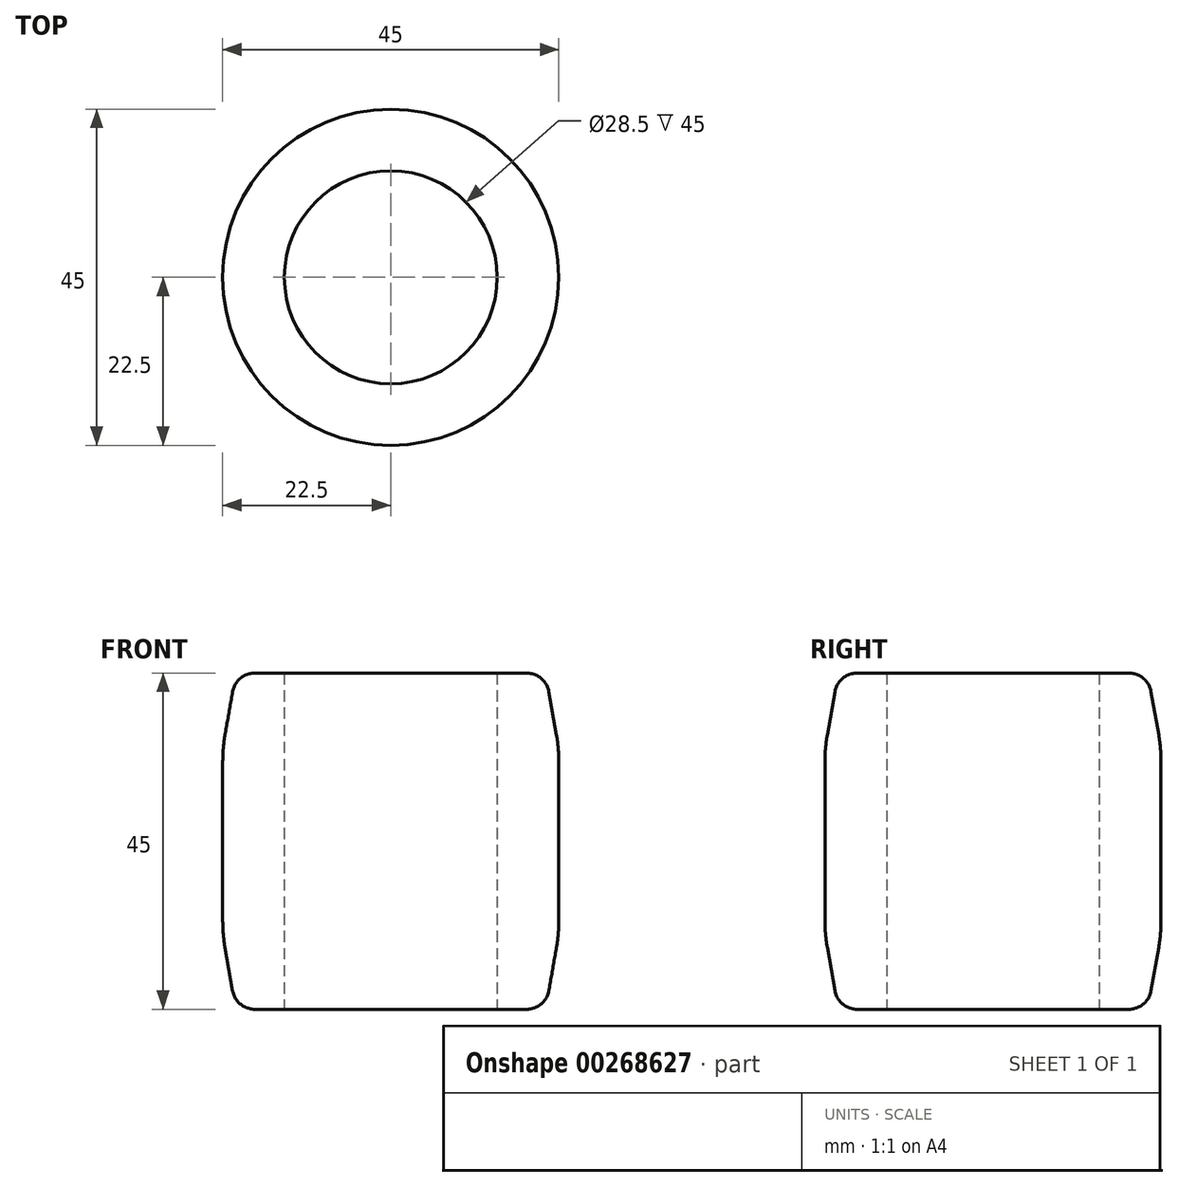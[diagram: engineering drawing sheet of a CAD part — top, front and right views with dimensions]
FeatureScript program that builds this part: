
annotation { "Feature Type Name" : "Feature", "Feature Type Description" : "" }
export const myFeature = defineFeature(function(context is Context, id is Id, definition is map)
    precondition{}
    {
        {
            var Q0;
            Q0=qCreatedBy(makeId("Top.planeOp"),FACE);
            var sketch = newSketch(context, id + "F0", { "sketchPlane" : qUnion([Q0])});
            skCircle(sketch, "E0", {"center": v(0, 0) * mm, "radius": 22.5 * mm});
            skCircle(sketch, "E1", {"center": v(0, 0) * mm, "radius": 14.25 * mm});
            skSolve(sketch);
        }
        {
            var Q0;
            Q0=makeQuery(id+"F0.imprint","IMPRINT",FACE,{"disambiguationData":[TD([[makeQuery(id+"F0.imprint","IMPRINT",EDGE,{"derivedFrom":sQuery(id+"F0.wireOp",EDGE,"E0")}),1.0]])]});
            extrude(context, id + "F1", {"entities" : qUnion([Q0]), "depth" : 45 * mm, "offsetDistance" : 25 * mm});
        }
        {
            var Q0;
            Q0=makeQuery(id+"F1.opExtrude","CAP_EDGE",EDGE,{"disambiguationData":[OSD([sQuery(id+"F0.wireOp",EDGE,"E0")])],"isStart":true});
            var Q1;
            Q1=makeQuery(id+"F1.opExtrude","CAP_EDGE",EDGE,{"disambiguationData":[OSD([sQuery(id+"F0.wireOp",EDGE,"E0")])],"isStart":false});
            chamfer(context, id + "F2", {"entities" : qUnion([Q0, Q1]), "chamferType" : ChamferType.OFFSET_ANGLE, "width" : 10 * mm, "oppositeDirection" : false, "angle" : 10 * degree, "tangentPropagation" : true});
        }
        {
            var Q0;
            Q0=makeQuery(id+"F1.opExtrude","SWEPT_FACE",FACE,{"disambiguationData":[OSD([sQuery(id+"F0.wireOp",EDGE,"E0")])]});
            var Q1;
            {var subQ0=sQuery(id+"F0.wireOp",EDGE,"E0");Q1=makeQuery(id+"F2.opChamfer","BLEND_EDGE",EDGE,{"blendedFrom":[makeQuery(id+"F1.opExtrude","CAP_EDGE",EDGE,{"disambiguationData":[OSD([subQ0])],"isStart":true}),makeQuery(id+"F1.opExtrude","SWEPT_FACE",FACE,{"disambiguationData":[OSD([subQ0])]})],"blendedInto":[makeQuery(id+"F1.opExtrude","SWEPT_FACE",FACE,{"disambiguationData":[OSD([subQ0])]})]});}
            fillet(context, id + "F3", {"entities" : qUnion([Q0, Q1]), "radius" : 20 * mm, "tangentPropagation" : true, "allowEdgeOverflow" : false});
        }
        {
            var Q0;
            {var subQ0=sQuery(id+"F0.wireOp",EDGE,"E0");Q0=makeQuery(id+"F2.opChamfer","BLEND_EDGE",EDGE,{"blendedFrom":[makeQuery(id+"F1.opExtrude","CAP_EDGE",EDGE,{"disambiguationData":[OSD([subQ0])],"isStart":false}),makeQuery(id+"F1.opExtrude","CAP_FACE",FACE,{"disambiguationData":[OSD([subQ0,sQuery(id+"F0.wireOp",EDGE,"E1")])],"isStart":false})],"blendedInto":[makeQuery(id+"F1.opExtrude","CAP_FACE",FACE,{"disambiguationData":[OSD([subQ0,sQuery(id+"F0.wireOp",EDGE,"E1")])],"isStart":false})]});}
            var Q1;
            {var subQ0=sQuery(id+"F0.wireOp",EDGE,"E0");Q1=makeQuery(id+"F2.opChamfer","BLEND_EDGE",EDGE,{"blendedFrom":[makeQuery(id+"F1.opExtrude","CAP_EDGE",EDGE,{"disambiguationData":[OSD([subQ0])],"isStart":true}),makeQuery(id+"F1.opExtrude","CAP_FACE",FACE,{"disambiguationData":[OSD([subQ0,sQuery(id+"F0.wireOp",EDGE,"E1")])],"isStart":true})],"blendedInto":[makeQuery(id+"F1.opExtrude","CAP_FACE",FACE,{"disambiguationData":[OSD([subQ0,sQuery(id+"F0.wireOp",EDGE,"E1")])],"isStart":true})]});}
            fillet(context, id + "F4", {"entities" : qUnion([Q0, Q1]), "radius" : 3 * mm, "tangentPropagation" : true, "allowEdgeOverflow" : false});
        }
    });
